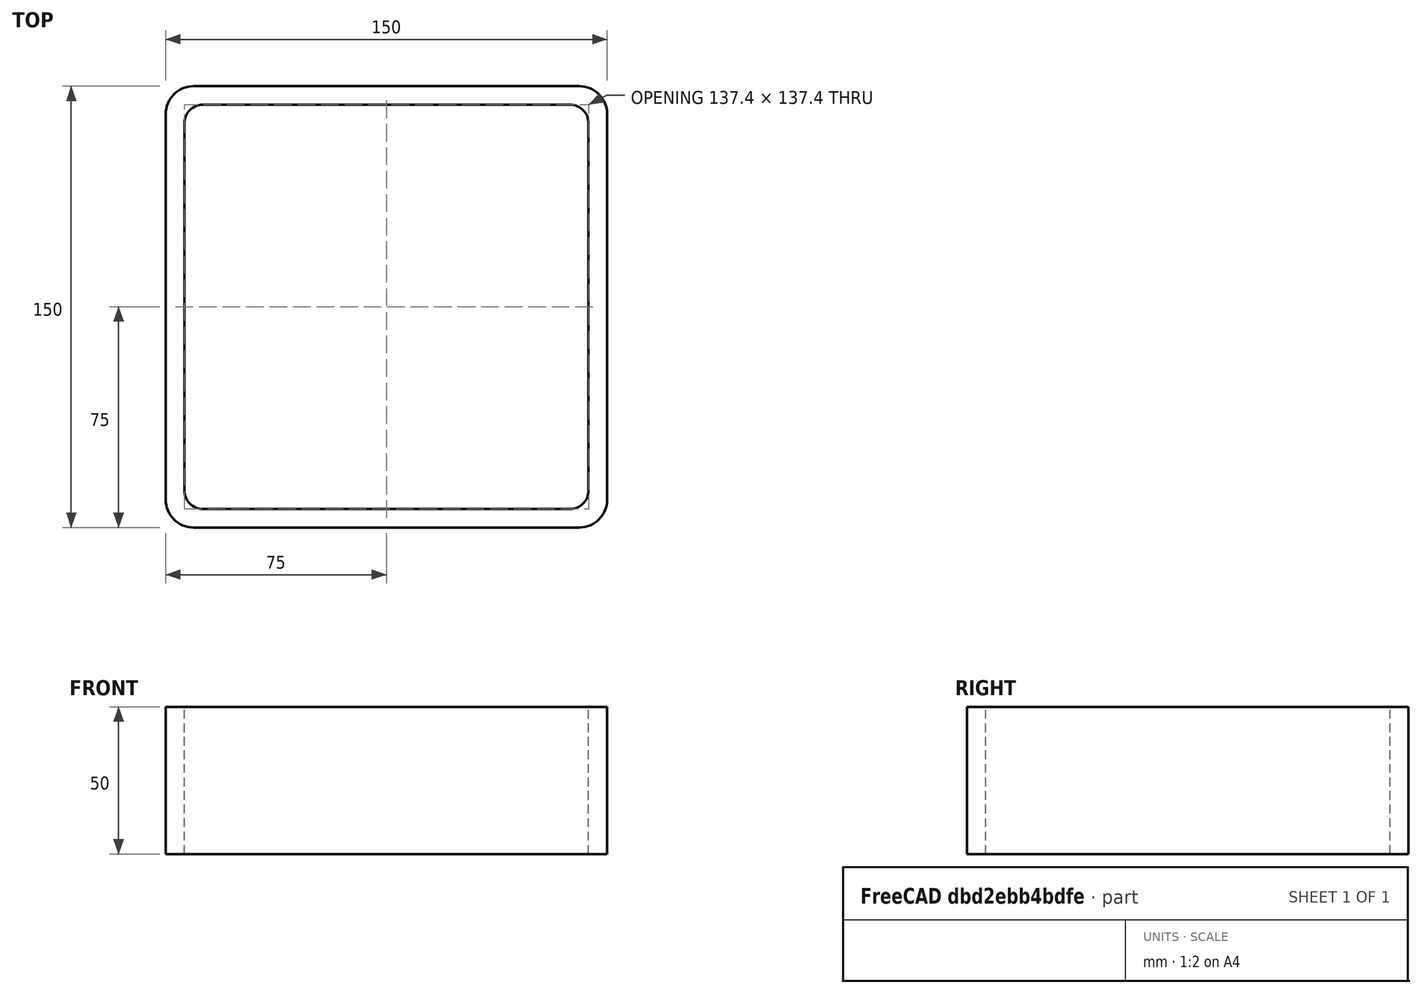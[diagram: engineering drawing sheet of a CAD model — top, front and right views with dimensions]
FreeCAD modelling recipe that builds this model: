
FCSTD DOCUMENT  (FreeCAD 0.15R4671 (Git))
Label: Square hollow section 150x150x6.3 EN10219 S235JRH
License: All rights reserved
LicenseURL: http://en.wikipedia.org/wiki/All_rights_reserved
objects: Sketcher::SketchObject×1, Part::Extrusion×1
note: 2 computed .brp shape members not serialized (recipe doc carries the construction recipe); baked Part::Feature solids carry a one-line shape summary decoded from their .brp

FEATURE [Sketcher::SketchObject] Sketch
  sketch-geometry (16):
    g0: LineSegment StartX=-62.4 StartY=68.7 StartZ=0 EndX=62.4 EndY=68.7 EndZ=0
    g1: LineSegment StartX=68.7 StartY=62.4 StartZ=0 EndX=68.7 EndY=-62.4 EndZ=0
    g2: LineSegment StartX=62.4 StartY=-68.7 StartZ=0 EndX=-62.4 EndY=-68.7 EndZ=0
    g3: LineSegment StartX=-68.7 StartY=-62.4 StartZ=0 EndX=-68.7 EndY=62.4 EndZ=0
    g4: LineSegment StartX=-65.55 StartY=75 StartZ=0 EndX=65.55 EndY=75 EndZ=0
    g5: LineSegment StartX=75 StartY=65.55 StartZ=0 EndX=75 EndY=-65.55 EndZ=0
    g6: LineSegment StartX=65.55 StartY=-75 StartZ=0 EndX=-65.55 EndY=-75 EndZ=0
    g7: LineSegment StartX=-75 StartY=-65.55 StartZ=0 EndX=-75 EndY=65.55 EndZ=0
    g8: ArcOfCircle CenterX=-62.4 CenterY=62.4 CenterZ=0 NormalX=0 NormalY=0 NormalZ=1 Radius=6.3 StartAngle=1.5708 EndAngle=3.14159
    g9: ArcOfCircle CenterX=62.4 CenterY=62.4 CenterZ=0 NormalX=0 NormalY=0 NormalZ=1 Radius=6.3 StartAngle=0 EndAngle=1.5708
    g10: ArcOfCircle CenterX=62.4 CenterY=-62.4 CenterZ=0 NormalX=0 NormalY=0 NormalZ=1 Radius=6.3 StartAngle=4.71239 EndAngle=6.28319
    g11: ArcOfCircle CenterX=-62.4 CenterY=-62.4 CenterZ=0 NormalX=0 NormalY=0 NormalZ=1 Radius=6.3 StartAngle=3.14159 EndAngle=4.71239
    g12: ArcOfCircle CenterX=65.55 CenterY=65.55 CenterZ=0 NormalX=0 NormalY=0 NormalZ=1 Radius=9.45 StartAngle=0 EndAngle=1.5708
    g13: ArcOfCircle CenterX=65.55 CenterY=-65.55 CenterZ=0 NormalX=0 NormalY=0 NormalZ=1 Radius=9.45 StartAngle=4.71239 EndAngle=6.28319
    g14: ArcOfCircle CenterX=-65.55 CenterY=-65.55 CenterZ=0 NormalX=0 NormalY=0 NormalZ=1 Radius=9.45 StartAngle=3.14159 EndAngle=4.71239
    g15: ArcOfCircle CenterX=-65.55 CenterY=65.55 CenterZ=0 NormalX=0 NormalY=0 NormalZ=1 Radius=9.45 StartAngle=1.5708 EndAngle=3.14159
  constraints (36):
    c: Horizontal(g2)
    c: Vertical(g3)
    c: Horizontal(g6)
    c: Vertical(g7)
    c: Tangent(g3,g8) = 1.5708
    c: Tangent(g0,g8) = 1.5708
    c: Tangent(g0,g9) = 1.5708
    c: Tangent(g1,g9) = 1.5708
    c: Tangent(g1,g10) = 1.5708
    c: Tangent(g2,g10) = 1.5708
    c: Tangent(g2,g11) = 1.5708
    c: Tangent(g3,g11) = 1.5708
    c: Tangent(g4,g12) = 1.5708
    c: Tangent(g5,g12) = 1.5708
    c: Tangent(g5,g13) = 1.5708
    c: Tangent(g6,g13) = 1.5708
    c: Tangent(g6,g14) = 1.5708
    c: Tangent(g7,g14) = 1.5708
    c: Tangent(g7,g15) = 1.5708
    c: Tangent(g4,g15) = 1.5708
    c: Equal(g9,g8)
    c: Equal(g9,g11)
    c: Equal(g9,g10)
    c: Equal(g12,g15)
    c: Equal(g12,g14)
    c: Equal(g12,g13)
    c: Symmetric(g4,g6,g-1)
    c: Symmetric(g7,g5,g-2)
    c: DistanceY(g4,g6) = -150
    c: DistanceX(g7,g5) = 150
    c: Symmetric(g3,g1,g-2)
    c: Symmetric(g0,g2,g-1)
    c: DistanceY(g0,g4) = 6.3
    c: DistanceX(g5,g1) = -6.3
    c: Radius(g9) = 6.3
    c: Radius(g12) = 9.45
FEATURE [Part::Extrusion] Extrude  label="Square hollow section 150x150x6.3 EN10219 S235JRH"
  Base = -> Sketch
  Dir = (0,0,50)
  Solid = true
